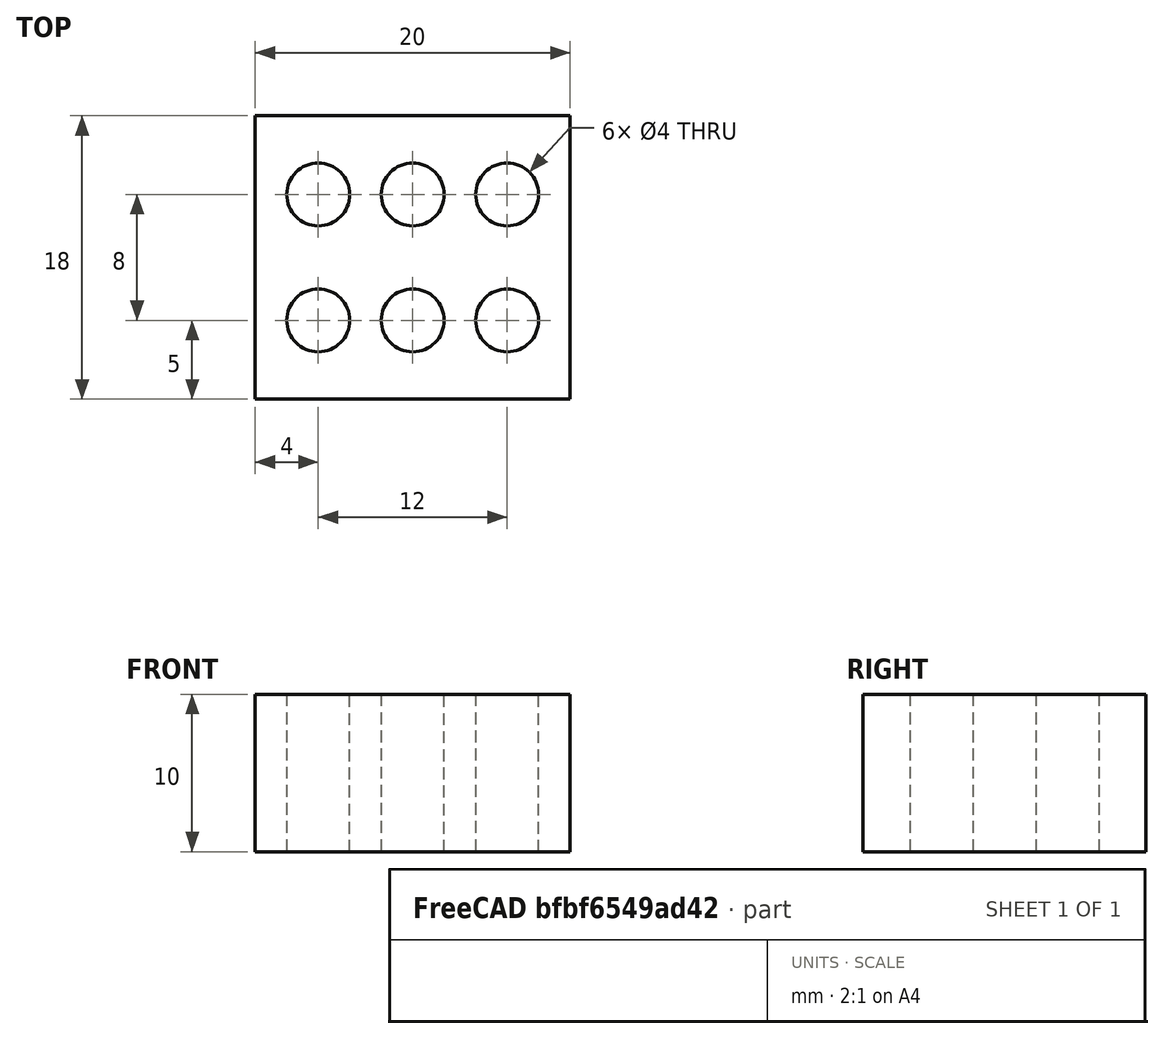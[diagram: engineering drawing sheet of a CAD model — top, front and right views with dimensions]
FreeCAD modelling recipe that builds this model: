
FCSTD DOCUMENT  (FreeCAD 0.21R33694 (Git))
Label: OJT1_T09R02_ladrillo
License: All rights reserved
LicenseURL: http://en.wikipedia.org/wiki/All_rights_reserved
objects: Part::Cylinder×6, Part::Cut×6, Part::Box×2, Part::MultiFuse×1
note: 15 computed .brp shape members not serialized (recipe doc carries the construction recipe); baked Part::Feature solids carry a one-line shape summary decoded from their .brp

FEATURE [Part::Box] Box  label="Cube"
  AttacherType = Attacher::AttachEngine3D
  Height = 10
  Length = 20
  Width = 10
FEATURE [Part::Cylinder] Cylinder
  Angle = 360
  AttacherType = Attacher::AttachEngine3D
  FirstAngle = 0
  Height = 10
  Placement = pos=(4,5,0) rot=(0,0,1;0rad)
  Radius = 2
  SecondAngle = 0
FEATURE [Part::Cylinder] Cylinder001
  Angle = 360
  AttacherType = Attacher::AttachEngine3D
  FirstAngle = 0
  Height = 10
  Placement = pos=(10,5,0) rot=(0,0,1;0rad)
  Radius = 2
  SecondAngle = 0
FEATURE [Part::Cylinder] Cylinder002
  Angle = 360
  AttacherType = Attacher::AttachEngine3D
  FirstAngle = 0
  Height = 10
  Placement = pos=(16,5,0) rot=(0,0,1;0rad)
  Radius = 2
  SecondAngle = 0
FEATURE [Part::Cut] Cut
  Base = -> Box
  Refine = true
  Tool = -> Cylinder
FEATURE [Part::Cut] Cut001
  Base = -> Cut
  Refine = true
  Tool = -> Cylinder002
FEATURE [Part::Cut] Cut002
  Base = -> Cut001
  Placement = pos=(0,9,0) rot=(0,0,1;0rad)
  Refine = true
  Tool = -> Cylinder001
FEATURE [Part::Box] Box001  label="Cube001"
  AttacherType = Attacher::AttachEngine3D
  Height = 10
  Length = 20
  Width = 10
FEATURE [Part::Cylinder] Cylinder003
  Angle = 360
  AttacherType = Attacher::AttachEngine3D
  FirstAngle = 0
  Height = 10
  Placement = pos=(4,5,0) rot=(0,0,1;0rad)
  Radius = 2
  SecondAngle = 0
FEATURE [Part::Cut] Cut003
  Base = -> Box001
  Refine = true
  Tool = -> Cylinder003
FEATURE [Part::Cylinder] Cylinder004
  Angle = 360
  AttacherType = Attacher::AttachEngine3D
  FirstAngle = 0
  Height = 10
  Placement = pos=(10,5,0) rot=(0,0,1;0rad)
  Radius = 2
  SecondAngle = 0
FEATURE [Part::Cylinder] Cylinder005
  Angle = 360
  AttacherType = Attacher::AttachEngine3D
  FirstAngle = 0
  Height = 10
  Placement = pos=(16,5,0) rot=(0,0,1;0rad)
  Radius = 2
  SecondAngle = 0
FEATURE [Part::Cut] Cut004
  Base = -> Cut003
  Refine = true
  Tool = -> Cylinder005
FEATURE [Part::Cut] Cut005
  Base = -> Cut004
  Placement = pos=(0,1,0) rot=(0,0,1;0rad)
  Refine = true
  Tool = -> Cylinder004
FEATURE [Part::MultiFuse] Fusion
  Refine = true
  Shapes = -> [Cut005,Cut002]
